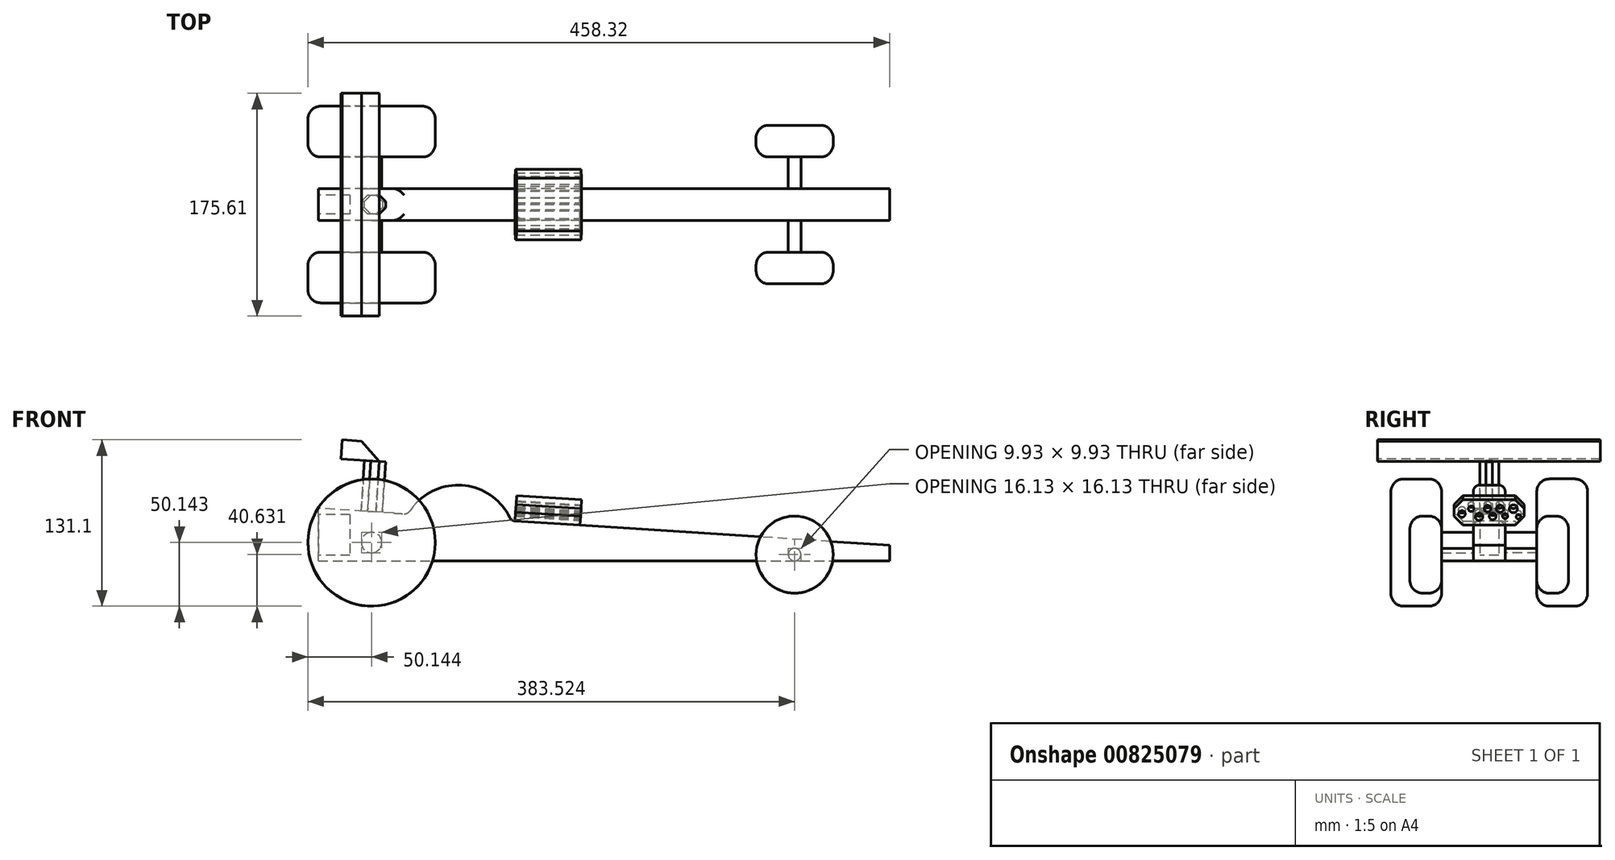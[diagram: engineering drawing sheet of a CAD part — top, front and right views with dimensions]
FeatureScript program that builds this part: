
annotation { "Feature Type Name" : "Feature", "Feature Type Description" : "" }
export const myFeature = defineFeature(function(context is Context, id is Id, definition is map)
    precondition{}
    {
        {
            var Q0;
            Q0=qCreatedBy(makeId("Front.planeOp"),FACE);
            var sketch = newSketch(context, id + "F0", { "sketchPlane" : qUnion([Q0])});
            skLineSegment(sketch, "E0", {"start": v(0, 0) * mm, "end": v(0, 41.59) * mm});
            skLineSegment(sketch, "E1", {"start": v(0, 0) * mm, "end": v(450.18, 0) * mm});
            skLineSegment(sketch, "E2", {"start": v(450.18, 0) * mm, "end": v(450.18, 12.36) * mm});
            skLineSegment(sketch, "E3", {"start": v(450.18, 12.36) * mm, "end": v(0, 41.59) * mm});
            skLineSegment(sketch, "E4", {"start": v(0, 41.59) * mm, "end": v(70.67, 37) * mm});
            skArc(sketch, "E5", {"start": v(152.02, 31.72) * mm, "mid": v(112.99, 59.7) * mm, "end": v(70.67, 37) * mm});
            skSolve(sketch);
        }
        {
            var Q0;
            {var subQ0=sQuery(id+"F0.wireOp",EDGE,"E5");var subQ6=sQuery(id+"F0.wireOp",EDGE,"E0");Q0=qUnion([makeQuery(id+"F0.imprint","IMPRINT",FACE,{"disambiguationData":[TD([[makeQuery(id+"F0.imprint","IMPRINT",EDGE,{"derivedFrom":subQ6}),-1.0]])]}),makeQuery(id+"F0.imprint","IMPRINT",FACE,{"disambiguationData":[TD([[makeQuery(id+"F0.imprint","IMPRINT",EDGE,{"derivedFrom":subQ0}),1.0]])]})]);}
            extrude(context, id + "F1", {"entities" : qUnion([Q0]), "depth" : 25 * mm, "offsetDistance" : 25 * mm});
        }
        {
            var Q0;
            Q0=makeQuery(id+"F1.opExtrude","CAP_EDGE",EDGE,{"disambiguationData":[OSD([sQuery(id+"F0.wireOp",EDGE,"E5")])],"isStart":false});
            var Q1;
            Q1=makeQuery(id+"F1.opExtrude","CAP_EDGE",EDGE,{"disambiguationData":[OSD([sQuery(id+"F0.wireOp",EDGE,"E5")])],"isStart":true});
            var Q2;
            {var subQ0=sQuery(id+"F0.wireOp",EDGE,"E5");var subQ1=sQuery(id+"F0.wireOp",EDGE,"E3");Q2=makeQuery(id+"F1.opExtrude","SWEPT_EDGE",EDGE,{"disambiguationData":[OSD([subQ1,subQ0]),TDD([makeQuery(id+"F0.imprint","INTERSECT",VERTEX,{"disambiguationData":[OD(0.0)],"derivedFrom":[subQ1,subQ0]})])]});}
            var Q3;
            {var subQ0=sQuery(id+"F0.wireOp",EDGE,"E5");var subQ1=sQuery(id+"F0.wireOp",EDGE,"E3");Q3=makeQuery(id+"F1.opExtrude","SWEPT_EDGE",EDGE,{"disambiguationData":[OSD([subQ1,subQ0]),TDD([makeQuery(id+"F0.imprint","INTERSECT",VERTEX,{"disambiguationData":[OD(1.0)],"derivedFrom":[subQ1,subQ0]})])]});}
            fillet(context, id + "F2", {"entities" : qUnion([Q0, Q1, Q2, Q3]), "radius" : 5 * mm, "tangentPropagation" : true, "allowEdgeOverflow" : false});
        }
        {
            var Q0;
            {var subQ0=sQuery(id+"F0.wireOp",EDGE,"E3");Q0=makeQuery(id+"F1.opExtrude","SWEPT_FACE",FACE,{"disambiguationData":[OSD([subQ0]),TDD([makeQuery(id+"F0.imprint","IMPRINT",EDGE,{"disambiguationData":[TD([[makeQuery(id+"F0.imprint","INTERSECT",VERTEX,{"derivedFrom":[sQuery(id+"F0.wireOp",EDGE,"E2"),subQ0]}),-1.0]])],"derivedFrom":subQ0})])]});}
            var sketch = newSketch(context, id + "F3", { "sketchPlane" : qUnion([Q0])});
            skLineSegment(sketch, "E6", {"start": v(152.65, -20) * mm, "end": v(203.94, -20) * mm});
            skLineSegment(sketch, "E7", {"start": v(203.94, -20) * mm, "end": v(203.94, -5) * mm});
            skLineSegment(sketch, "E8", {"start": v(203.94, -5) * mm, "end": v(203.94, 15.2) * mm});
            skLineSegment(sketch, "E9", {"start": v(203.94, -20) * mm, "end": v(203.94, -40.34) * mm});
            skLineSegment(sketch, "E10", {"start": v(203.94, -40.34) * mm, "end": v(152.65, -40.34) * mm});
            skLineSegment(sketch, "E11", {"start": v(152.65, -40.34) * mm, "end": v(152.65, 15.2) * mm});
            skLineSegment(sketch, "E12", {"start": v(152.65, 15.2) * mm, "end": v(203.94, 15.2) * mm});
            skSolve(sketch);
        }
        {
            var Q0;
            Q0 = qSketchRegion(id + "F3", true);
            extrude(context, id + "F4", {"entities" : qUnion([Q0]), "operationType" : NewBodyOperationType.ADD, "depth" : 20 * mm, "offsetDistance" : 25 * mm});
        }
        {
            var Q0;
            Q0=makeQuery(id+"F4.opExtrude","CAP_EDGE",EDGE,{"disambiguationData":[OSD([sQuery(id+"F3.wireOp",EDGE,"E10")])],"isStart":false});
            var Q1;
            Q1=makeQuery(id+"F4.opExtrude","CAP_EDGE",EDGE,{"disambiguationData":[OSD([sQuery(id+"F3.wireOp",EDGE,"E10")])],"isStart":true});
            var Q2;
            Q2=makeQuery(id+"F4.opExtrude","CAP_EDGE",EDGE,{"disambiguationData":[OSD([sQuery(id+"F3.wireOp",EDGE,"E12")])],"isStart":false});
            var Q3;
            Q3=makeQuery(id+"F4.opExtrude","CAP_EDGE",EDGE,{"disambiguationData":[OSD([sQuery(id+"F3.wireOp",EDGE,"E12")])],"isStart":true});
            chamfer(context, id + "F5", {"entities" : qUnion([Q0, Q1, Q2, Q3]), "width" : 7 * mm, "tangentPropagation" : true});
        }
        {
            var Q0;
            Q0=makeQuery(id+"F4.opExtrude","SWEPT_FACE",FACE,{"disambiguationData":[OSD([sQuery(id+"F3.wireOp",EDGE,"E7"),sQuery(id+"F3.wireOp",EDGE,"E8"),sQuery(id+"F3.wireOp",EDGE,"E9")])]});
            var sketch = newSketch(context, id + "F6", { "sketchPlane" : qUnion([Q0])});
            skCircle(sketch, "E13", {"center": v(-34.01, 50.4) * mm, "radius": 2.62 * mm});
            skCircle(sketch, "E14", {"center": v(-26.72, 54.5) * mm, "radius": 2.22 * mm});
            skCircle(sketch, "E15", {"center": v(-20.44, 48.12) * mm, "radius": 2.91 * mm});
            skCircle(sketch, "E16", {"center": v(-13.83, 54.5) * mm, "radius": 2.65 * mm});
            skCircle(sketch, "E17", {"center": v(-9.79, 48.43) * mm, "radius": 2.66 * mm});
            skCircle(sketch, "E18", {"center": v(-4, 54.5) * mm, "radius": 2.9 * mm});
            skCircle(sketch, "E19", {"center": v(0, 48.67) * mm, "radius": 2.03 * mm});
            skCircle(sketch, "E20", {"center": v(6.56, 54.5) * mm, "radius": 3.16 * mm});
            skCircle(sketch, "E21", {"center": v(10.64, 48.07) * mm, "radius": 1.84 * mm});
            skSolve(sketch);
        }
        {
            var Q0;
            Q0 = qSketchRegion(id + "F6", true);
            extrude(context, id + "F7", {"entities" : qUnion([Q0]), "operationType" : NewBodyOperationType.REMOVE, "oppositeDirection" : true, "depth" : 55 * mm, "offsetDistance" : 25 * mm});
        }
        {
            var Q0;
            Q0=makeQuery(id+"F1.opExtrude","CAP_FACE",FACE,{"disambiguationData":[OSD([sQuery(id+"F0.wireOp",EDGE,"E0"),sQuery(id+"F0.wireOp",EDGE,"E1"),sQuery(id+"F0.wireOp",EDGE,"E2"),sQuery(id+"F0.wireOp",EDGE,"E3"),sQuery(id+"F0.wireOp",EDGE,"E5")])],"isStart":true});
            var sketch = newSketch(context, id + "F8", { "sketchPlane" : qUnion([Q0])});
            skCircle(sketch, "E22", {"center": v(-42, 14.52) * mm, "radius": 8.06 * mm});
            skCircle(sketch, "E23", {"center": v(-375.38, 5.01) * mm, "radius": 4.96 * mm});
            skSolve(sketch);
        }
        {
            var Q0;
            Q0 = qSketchRegion(id + "F8", true);
            extrude(context, id + "F9", {"entities" : qUnion([Q0]), "operationType" : NewBodyOperationType.ADD, "depth" : 25 * mm, "offsetDistance" : 25 * mm});
        }
        {
            var Q0;
            Q0 = qSketchRegion(id + "F8", true);
            extrude(context, id + "F10", {"entities" : qUnion([Q0]), "operationType" : NewBodyOperationType.ADD, "oppositeDirection" : true, "depth" : 50 * mm, "offsetDistance" : 25 * mm});
        }
        {
            var Q0;
            Q0=makeQuery(id+"F9.opExtrude","CAP_FACE",FACE,{"disambiguationData":[OSD([sQuery(id+"F8.wireOp",EDGE,"E23")])],"isStart":false});
            var sketch = newSketch(context, id + "F11", { "sketchPlane" : qUnion([Q0])});
            skCircle(sketch, "E24", {"center": v(-375.38, 5.01) * mm, "radius": 30.44 * mm});
            skSolve(sketch);
        }
        {
            var Q0;
            Q0 = qSketchRegion(id + "F11", true);
            extrude(context, id + "F12", {"entities" : qUnion([Q0]), "operationType" : NewBodyOperationType.ADD, "depth" : 25 * mm, "offsetDistance" : 25 * mm});
        }
        {
            var Q0;
            Q0=makeQuery(id+"F10.opExtrude","CAP_FACE",FACE,{"disambiguationData":[OSD([sQuery(id+"F8.wireOp",EDGE,"E23")])],"isStart":false});
            var sketch = newSketch(context, id + "F13", { "sketchPlane" : qUnion([Q0])});
            skCircle(sketch, "E25", {"center": v(375.38, 5.01) * mm, "radius": 30.35 * mm});
            skSolve(sketch);
        }
        {
            var Q0;
            Q0 = qSketchRegion(id + "F13", true);
            extrude(context, id + "F14", {"entities" : qUnion([Q0]), "operationType" : NewBodyOperationType.ADD, "depth" : 25 * mm, "offsetDistance" : 25 * mm});
        }
        {
            var Q0;
            Q0=makeQuery(id+"F10.opExtrude","CAP_FACE",FACE,{"disambiguationData":[OSD([sQuery(id+"F8.wireOp",EDGE,"E22")])],"isStart":false});
            var sketch = newSketch(context, id + "F15", { "sketchPlane" : qUnion([Q0])});
            skCircle(sketch, "E26", {"center": v(42, 14.52) * mm, "radius": 50.12 * mm});
            skSolve(sketch);
        }
        {
            var Q0;
            Q0 = qSketchRegion(id + "F15", true);
            extrude(context, id + "F16", {"entities" : qUnion([Q0]), "operationType" : NewBodyOperationType.ADD, "depth" : 40 * mm, "offsetDistance" : 25 * mm});
        }
        {
            var Q0;
            Q0=makeQuery(id+"F9.opExtrude","CAP_FACE",FACE,{"disambiguationData":[OSD([sQuery(id+"F8.wireOp",EDGE,"E22")])],"isStart":false});
            var sketch = newSketch(context, id + "F17", { "sketchPlane" : qUnion([Q0])});
            skCircle(sketch, "E27", {"center": v(-42, 14.52) * mm, "radius": 50.14 * mm});
            skSolve(sketch);
        }
        {
            var Q0;
            Q0 = qSketchRegion(id + "F17", true);
            extrude(context, id + "F18", {"entities" : qUnion([Q0]), "operationType" : NewBodyOperationType.ADD, "depth" : 40 * mm, "offsetDistance" : 25 * mm});
        }
        {
            var Q0;
            Q0=makeQuery(id+"F18.opExtrude","CAP_EDGE",EDGE,{"disambiguationData":[OSD([sQuery(id+"F17.wireOp",EDGE,"E27")])],"isStart":false});
            var Q1;
            Q1=makeQuery(id+"F18.opExtrude","CAP_EDGE",EDGE,{"disambiguationData":[OSD([sQuery(id+"F17.wireOp",EDGE,"E27")])],"isStart":true});
            var Q2;
            Q2=makeQuery(id+"F16.opExtrude","CAP_EDGE",EDGE,{"disambiguationData":[OSD([sQuery(id+"F15.wireOp",EDGE,"E26")])],"isStart":true});
            var Q3;
            Q3=makeQuery(id+"F16.opExtrude","CAP_EDGE",EDGE,{"disambiguationData":[OSD([sQuery(id+"F15.wireOp",EDGE,"E26")])],"isStart":false});
            var Q4;
            Q4=makeQuery(id+"F14.opExtrude","CAP_EDGE",EDGE,{"disambiguationData":[OSD([sQuery(id+"F13.wireOp",EDGE,"E25")])],"isStart":false});
            var Q5;
            Q5=makeQuery(id+"F14.opExtrude","CAP_EDGE",EDGE,{"disambiguationData":[OSD([sQuery(id+"F13.wireOp",EDGE,"E25")])],"isStart":true});
            var Q6;
            Q6=makeQuery(id+"F12.opExtrude","CAP_EDGE",EDGE,{"disambiguationData":[OSD([sQuery(id+"F11.wireOp",EDGE,"E24")])],"isStart":true});
            var Q7;
            Q7=makeQuery(id+"F12.opExtrude","CAP_EDGE",EDGE,{"disambiguationData":[OSD([sQuery(id+"F11.wireOp",EDGE,"E24")])],"isStart":false});
            fillet(context, id + "F19", {"entities" : qUnion([Q0, Q1, Q2, Q3, Q4, Q5, Q6, Q7]), "radius" : 10 * mm, "tangentPropagation" : true, "allowEdgeOverflow" : false});
        }
        {
            var Q0;
            Q0=makeQuery(id+"F1.opExtrude","SWEPT_FACE",FACE,{"disambiguationData":[OSD([sQuery(id+"F0.wireOp",EDGE,"E0")])]});
            var sketch = newSketch(context, id + "F20", { "sketchPlane" : qUnion([Q0])});
            skPoint(sketch, "E28.oppositeSnap0", {"position": v(20, 31.57) * mm});
            skLineSegment(sketch, "E28.bottom", {"start": v(5, 36.58) * mm, "end": v(20, 36.58) * mm});
            skLineSegment(sketch, "E28.top", {"start": v(5, 4.62) * mm, "end": v(20, 4.62) * mm});
            skLineSegment(sketch, "E28.left", {"start": v(5, 36.58) * mm, "end": v(5, 4.62) * mm});
            skLineSegment(sketch, "E28.right", {"start": v(20, 36.58) * mm, "end": v(20, 4.62) * mm});
            skSolve(sketch);
        }
        {
            var Q0;
            Q0 = qSketchRegion(id + "F20", true);
            extrude(context, id + "F21", {"entities" : qUnion([Q0]), "operationType" : NewBodyOperationType.REMOVE, "oppositeDirection" : true, "depth" : 25 * mm, "offsetDistance" : 25 * mm});
        }
        {
            var Q0;
            {var subQ0=sQuery(id+"F0.wireOp",EDGE,"E3");Q0=makeQuery(id+"F1.opExtrude","SWEPT_FACE",FACE,{"disambiguationData":[OSD([subQ0]),TDD([makeQuery(id+"F0.imprint","IMPRINT",EDGE,{"disambiguationData":[TD([[makeQuery(id+"F0.imprint","INTERSECT",VERTEX,{"derivedFrom":[sQuery(id+"F0.wireOp",EDGE,"E0"),subQ0]}),1.0]])],"derivedFrom":subQ0})])]});}
            var sketch = newSketch(context, id + "F22", { "sketchPlane" : qUnion([Q0])});
            skLineSegment(sketch, "E29", {"start": v(47.86, -5) * mm, "end": v(47.86, -20) * mm});
            skLineSegment(sketch, "E30", {"start": v(47.86, -20) * mm, "end": v(31.21, -20) * mm});
            skLineSegment(sketch, "E31", {"start": v(31.21, -20) * mm, "end": v(31.21, -5) * mm});
            skLineSegment(sketch, "E32", {"start": v(31.21, -5) * mm, "end": v(47.86, -5) * mm});
            skSolve(sketch);
        }
        {
            var Q0;
            Q0 = qSketchRegion(id + "F22", true);
            extrude(context, id + "F23", {"entities" : qUnion([Q0]), "operationType" : NewBodyOperationType.ADD, "depth" : 40 * mm, "offsetDistance" : 25 * mm});
        }
        {
            var Q0;
            Q0=makeQuery(id+"F23.opExtrude","SWEPT_EDGE",EDGE,{"disambiguationData":[OSD([sQuery(id+"F0.wireOp",EDGE,"E3"),sQuery(id+"F22.wireOp",EDGE,"E31"),sQuery(id+"F22.wireOp",EDGE,"E32")])]});
            var Q1;
            Q1=makeQuery(id+"F23.opExtrude","SWEPT_EDGE",EDGE,{"disambiguationData":[OSD([sQuery(id+"F0.wireOp",EDGE,"E3"),sQuery(id+"F22.wireOp",EDGE,"E29"),sQuery(id+"F22.wireOp",EDGE,"E32")])]});
            var Q2;
            Q2=makeQuery(id+"F23.opExtrude","SWEPT_EDGE",EDGE,{"disambiguationData":[OSD([sQuery(id+"F0.wireOp",EDGE,"E3"),sQuery(id+"F22.wireOp",EDGE,"E29"),sQuery(id+"F22.wireOp",EDGE,"E30")])]});
            var Q3;
            Q3=makeQuery(id+"F23.opExtrude","SWEPT_EDGE",EDGE,{"disambiguationData":[OSD([sQuery(id+"F0.wireOp",EDGE,"E3"),sQuery(id+"F22.wireOp",EDGE,"E30"),sQuery(id+"F22.wireOp",EDGE,"E31")])]});
            chamfer(context, id + "F24", {"entities" : qUnion([Q0, Q1, Q2, Q3]), "width" : 5 * mm, "tangentPropagation" : true});
        }
        {
            var Q0;
            Q0=makeQuery(id+"F23.opExtrude","CAP_FACE",FACE,{"disambiguationData":[OSD([sQuery(id+"F22.wireOp",EDGE,"E29"),sQuery(id+"F22.wireOp",EDGE,"E30"),sQuery(id+"F22.wireOp",EDGE,"E31"),sQuery(id+"F22.wireOp",EDGE,"E32")])],"isStart":false});
            var sketch = newSketch(context, id + "F25", { "sketchPlane" : qUnion([Q0])});
            skLineSegment(sketch, "E33", {"start": v(42.86, -20) * mm, "end": v(42.86, -100.42) * mm});
            skLineSegment(sketch, "E34", {"start": v(42.86, -5) * mm, "end": v(42.86, 75.2) * mm});
            skLineSegment(sketch, "E35", {"start": v(42.86, 75.2) * mm, "end": v(12.6, 75.2) * mm});
            skLineSegment(sketch, "E36", {"start": v(12.6, 75.2) * mm, "end": v(12.6, -100.42) * mm});
            skLineSegment(sketch, "E37", {"start": v(12.6, -100.42) * mm, "end": v(42.86, -100.42) * mm});
            skLineSegment(sketch, "E38", {"start": v(42.86, -5) * mm, "end": v(42.86, -20) * mm});
            skSolve(sketch);
        }
        {
            var Q0;
            Q0 = qSketchRegion(id + "F25", true);
            extrude(context, id + "F26", {"entities" : qUnion([Q0]), "operationType" : NewBodyOperationType.ADD, "depth" : 15 * mm, "offsetDistance" : 25 * mm});
        }
        {
            var Q0;
            Q0=makeQuery(id+"F26.opExtrude","CAP_EDGE",EDGE,{"disambiguationData":[OSD([sQuery(id+"F25.wireOp",EDGE,"E33"),sQuery(id+"F25.wireOp",EDGE,"E34"),sQuery(id+"F25.wireOp",EDGE,"E38")])],"isStart":false});
            chamfer(context, id + "F27", {"entities" : qUnion([Q0]), "width" : 15 * mm, "tangentPropagation" : true});
        }
    });
